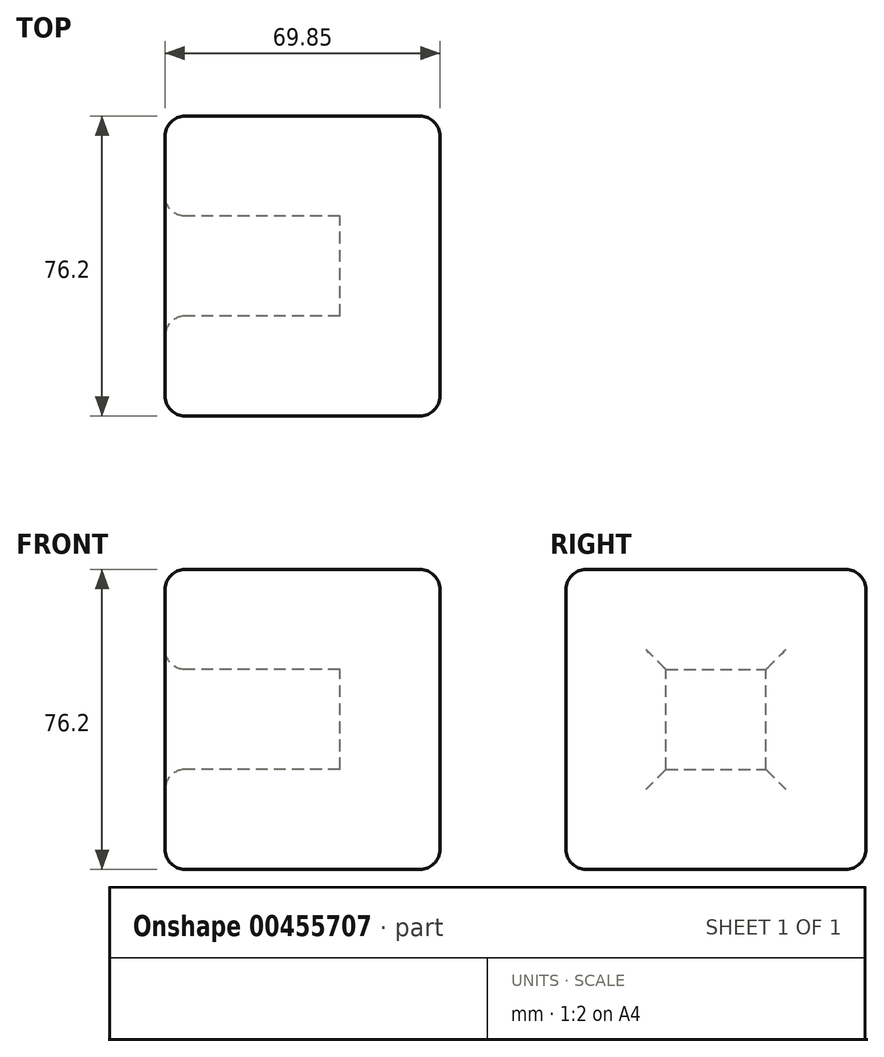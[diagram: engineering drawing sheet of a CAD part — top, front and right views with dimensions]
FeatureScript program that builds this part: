
annotation { "Feature Type Name" : "Feature", "Feature Type Description" : "" }
export const myFeature = defineFeature(function(context is Context, id is Id, definition is map)
    precondition{}
    {
        {
            var Q0;
            Q0=qCreatedBy(makeId("Right.planeOp"),FACE);
            var sketch = newSketch(context, id + "F0", { "sketchPlane" : qUnion([Q0])});
            skLineSegment(sketch, "E0.bottom", {"start": v(-38.1, -38.1) * mm, "end": v(38.1, -38.1) * mm});
            skLineSegment(sketch, "E0.top", {"start": v(-38.1, 38.1) * mm, "end": v(38.1, 38.1) * mm});
            skLineSegment(sketch, "E0.left", {"start": v(-38.1, -38.1) * mm, "end": v(-38.1, 38.1) * mm});
            skLineSegment(sketch, "E0.right", {"start": v(38.1, -38.1) * mm, "end": v(38.1, 38.1) * mm});
            skPoint(sketch, "E0.middle", {"position": v(0, 0) * mm});
            skSolve(sketch);
        }
        {
            var Q0;
            Q0=makeQuery(id+"F0.imprint","IMPRINT",FACE,{"disambiguationData":[TD([[makeQuery(id+"F0.imprint","IMPRINT",EDGE,{"derivedFrom":sQuery(id+"F0.wireOp",EDGE,"E0.bottom")}),1.0]])]});
            extrude(context, id + "F1", {"entities" : qUnion([Q0]), "depth" : 69.85 * mm});
        }
        {
            var Q0;
            Q0=makeQuery(id+"F1.opExtrude","CAP_FACE",FACE,{"disambiguationData":[OSD([sQuery(id+"F0.wireOp",EDGE,"E0.bottom"),sQuery(id+"F0.wireOp",EDGE,"E0.top"),sQuery(id+"F0.wireOp",EDGE,"E0.left"),sQuery(id+"F0.wireOp",EDGE,"E0.right")])],"isStart":true});
            shell(context, id + "F2", {"entities" : qUnion([Q0]), "thickness" : 25.4 * mm});
        }
        {
            var Q0;
            Q0=makeQuery(id+"F1.opExtrude","SWEPT_FACE",FACE,{"disambiguationData":[OSD([sQuery(id+"F0.wireOp",EDGE,"E0.right")])]});
            fillet(context, id + "F3", {"entities" : qUnion([Q0]), "radius" : 5.08 * mm, "tangentPropagation" : true, "allowEdgeOverflow" : false});
        }
        {
            var Q0;
            Q0=makeQuery(id+"F1.opExtrude","SWEPT_FACE",FACE,{"disambiguationData":[OSD([sQuery(id+"F0.wireOp",EDGE,"E0.left")])]});
            fillet(context, id + "F4", {"entities" : qUnion([Q0]), "radius" : 5.08 * mm, "tangentPropagation" : true, "allowEdgeOverflow" : false});
        }
        {
            var Q0;
            Q0=makeQuery(id+"F1.opExtrude","CAP_FACE",FACE,{"disambiguationData":[OSD([sQuery(id+"F0.wireOp",EDGE,"E0.bottom"),sQuery(id+"F0.wireOp",EDGE,"E0.top"),sQuery(id+"F0.wireOp",EDGE,"E0.left"),sQuery(id+"F0.wireOp",EDGE,"E0.right")])],"isStart":true});
            fillet(context, id + "F5", {"entities" : qUnion([Q0]), "radius" : 5.08 * mm, "tangentPropagation" : true, "allowEdgeOverflow" : false});
        }
        {
            var Q0;
            Q0=makeQuery(id+"F1.opExtrude","CAP_FACE",FACE,{"disambiguationData":[OSD([sQuery(id+"F0.wireOp",EDGE,"E0.bottom"),sQuery(id+"F0.wireOp",EDGE,"E0.top"),sQuery(id+"F0.wireOp",EDGE,"E0.left"),sQuery(id+"F0.wireOp",EDGE,"E0.right")])],"isStart":false});
            fillet(context, id + "F6", {"entities" : qUnion([Q0]), "radius" : 5.08 * mm, "tangentPropagation" : true, "allowEdgeOverflow" : false});
        }
    });
